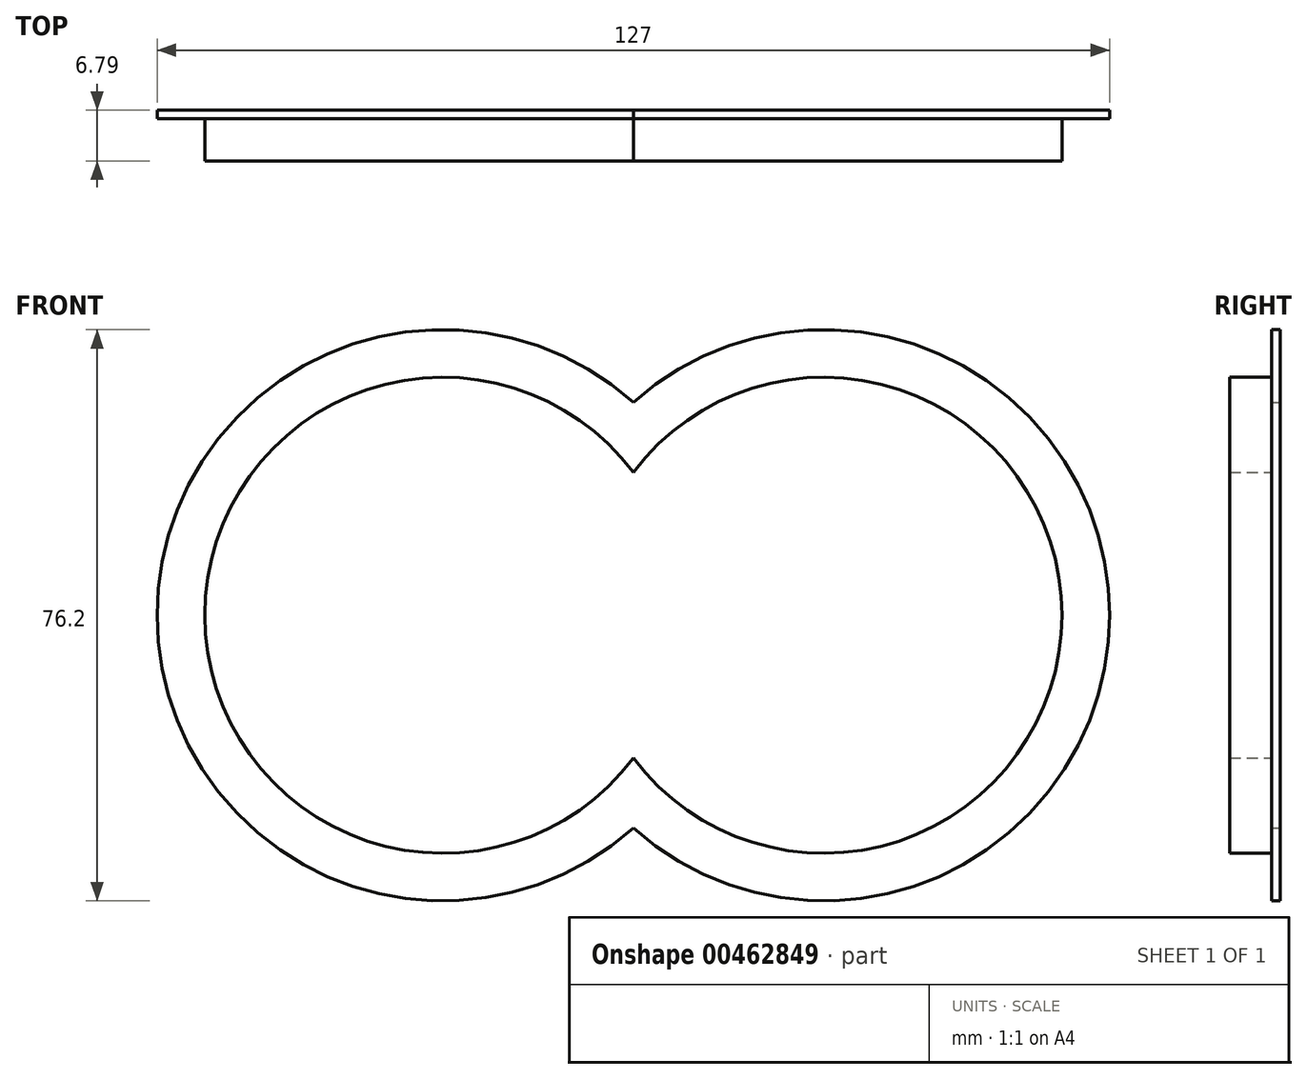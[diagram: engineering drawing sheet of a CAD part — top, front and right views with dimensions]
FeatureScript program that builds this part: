
annotation { "Feature Type Name" : "Feature", "Feature Type Description" : "" }
export const myFeature = defineFeature(function(context is Context, id is Id, definition is map)
    precondition{}
    {
        {
            var Q0;
            Q0=qCreatedBy(makeId("Front.planeOp"),FACE);
            var sketch = newSketch(context, id + "F0", { "sketchPlane" : qUnion([Q0])});
            skLineSegment(sketch, "E0", {"start": v(0, 48.85) * mm, "end": v(0, -60.36) * mm});
            skCircle(sketch, "E1", {"center": v(25.4, 0) * mm, "radius": 38.1 * mm});
            skCircle(sketch, "E2", {"center": v(-25.4, 0) * mm, "radius": 38.1 * mm});
            skSolve(sketch);
        }
        {
            var Q0;
            Q0 = qSketchRegion(id + "F0", true);
            extrude(context, id + "F1", {"entities" : qUnion([Q0]), "depth" : 0.57 * mm});
        }
        {
            var Q0;
            Q0=makeQuery(id+"F1.opExtrude","CAP_FACE",FACE,{"disambiguationData":[OSD([sQuery(id+"F0.wireOp",EDGE,"E1"),sQuery(id+"F0.wireOp",EDGE,"E2")])],"isStart":true});
            extrude(context, id + "F2", {"entities" : qUnion([Q0]), "operationType" : NewBodyOperationType.ADD, "depth" : 0.57 * mm});
        }
        {
            var Q0;
            Q0=makeQuery(id+"F1.opExtrude","CAP_FACE",FACE,{"disambiguationData":[OSD([sQuery(id+"F0.wireOp",EDGE,"E1"),sQuery(id+"F0.wireOp",EDGE,"E2")])],"isStart":false});
            var sketch = newSketch(context, id + "F3", { "sketchPlane" : qUnion([Q0])});
            skCircle(sketch, "E3", {"center": v(-25.4, 0) * mm, "radius": 31.75 * mm});
            skCircle(sketch, "E4", {"center": v(25.4, 0) * mm, "radius": 31.75 * mm});
            skSolve(sketch);
        }
        {
            var Q0;
            Q0 = qSketchRegion(id + "F3", true);
            extrude(context, id + "F4", {"entities" : qUnion([Q0]), "operationType" : NewBodyOperationType.ADD, "depth" : 5.64 * mm});
        }
    });
